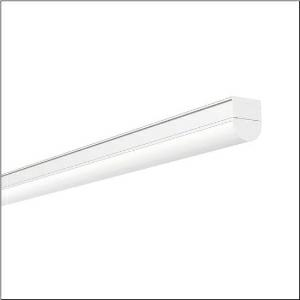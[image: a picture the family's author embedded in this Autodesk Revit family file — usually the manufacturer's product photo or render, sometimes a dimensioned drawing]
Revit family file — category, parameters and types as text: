
# Revit family: ecopack_31_51lj12mdm20a
name_source: partatom
category: Lighting Fixtures
units: mm (PartAtom-declared; Revit-internal decimal feet)

## family parameters
Cut with Voids When Loaded = No
Host = Face
Light Source = No
Part Type = Normal
Room Calculation Point = No
Round Connector Dimension = Use Diameter
Shared = No

## types (1)
- --- (1 x LED, 2510 lm, 20 W, 5000K)
    Apparent Load = 20 VA
    CIE Flux Codes = 41 71 90 93 100
    Color Rendering = 80
    Color Temperature = 5000K
    Default Elevation = 1800 mm
    Description = Ecopack 31, diffuser luminaire, primary optical cover: cover, of PC, frosted, light emission: direct distribution, primary light characteristic: symmetric, installation type: surface-mounted, LED, rated luminous flux: 2.600lm, luminous efficacy: 130lm/W, light colour: 830/840/850, colour temperature: 3000/4000/5000K, control gear: ON/OFF Multilumen, with terminal, 3-pole, mains connection: 220..240V, AC, 50/60Hz, rated input power: 20W, housing, of aluminium, traffic white (RAL 9016), length: 600mm, width: 56mm, height: 68mm, end cap, of PC, white, protection rating (complete): IP20, insulation class (complete): insulation class I (protective earthing), certification: CE, impact resistance: IK06, permissible operating ambient temperature: -20..+40°C, packaging unit: 1 piece
    Height = 68 mm
    Lamp = 1 x LED
    Lamp Light Flux = 2510 lm
    Lamp Power = 20 W
    Lamp count = 1
    Length = 600 mm
    Luminous efficacy = 126 lm/W
    Manufacturer = Siteco
    ModVariant = No
    Model = 51LJ12MDM20A
    Mounting Place = Ceiling
    Mounting Type = Surface mounted
    Number of Poles = 1
    OnlyDefault = Yes
    Power Factor = 1
    Product Name = Ecopack 31
    Product group = diffuser luminaire
    ProductGroupID = 307
    Protection Class = Protection class I
    Protection Degree = IP 20
    RLX_Detail_Level = 1
    RLX_Emergency_Light_Flux = 0 lm
    RLX_Emergency_Type = 0
    RLX_Emergency_Type_DB = No
    RlxData = <blob elided: 25401 chars, md5=32d452f9>
    Socket = socket
    Standby Power = 0 W
    System Light Flux = 2510 lm
    System Power = 20 W
    Type Comments = individual setting: colour temperature 5000K, luminous flux: 100 % | (ON | ON)
    Type Image = l_1007030.jpg
    URL = http://relux.com
    VarID = @adj_173541
    Voltage = 0 V
    Weight = 0.00 kg
    Width = 56 mm

## geometry (parser evidence)
native form markers: Blend x4, Sweep x14
no freeform markers — native parametric forms only
